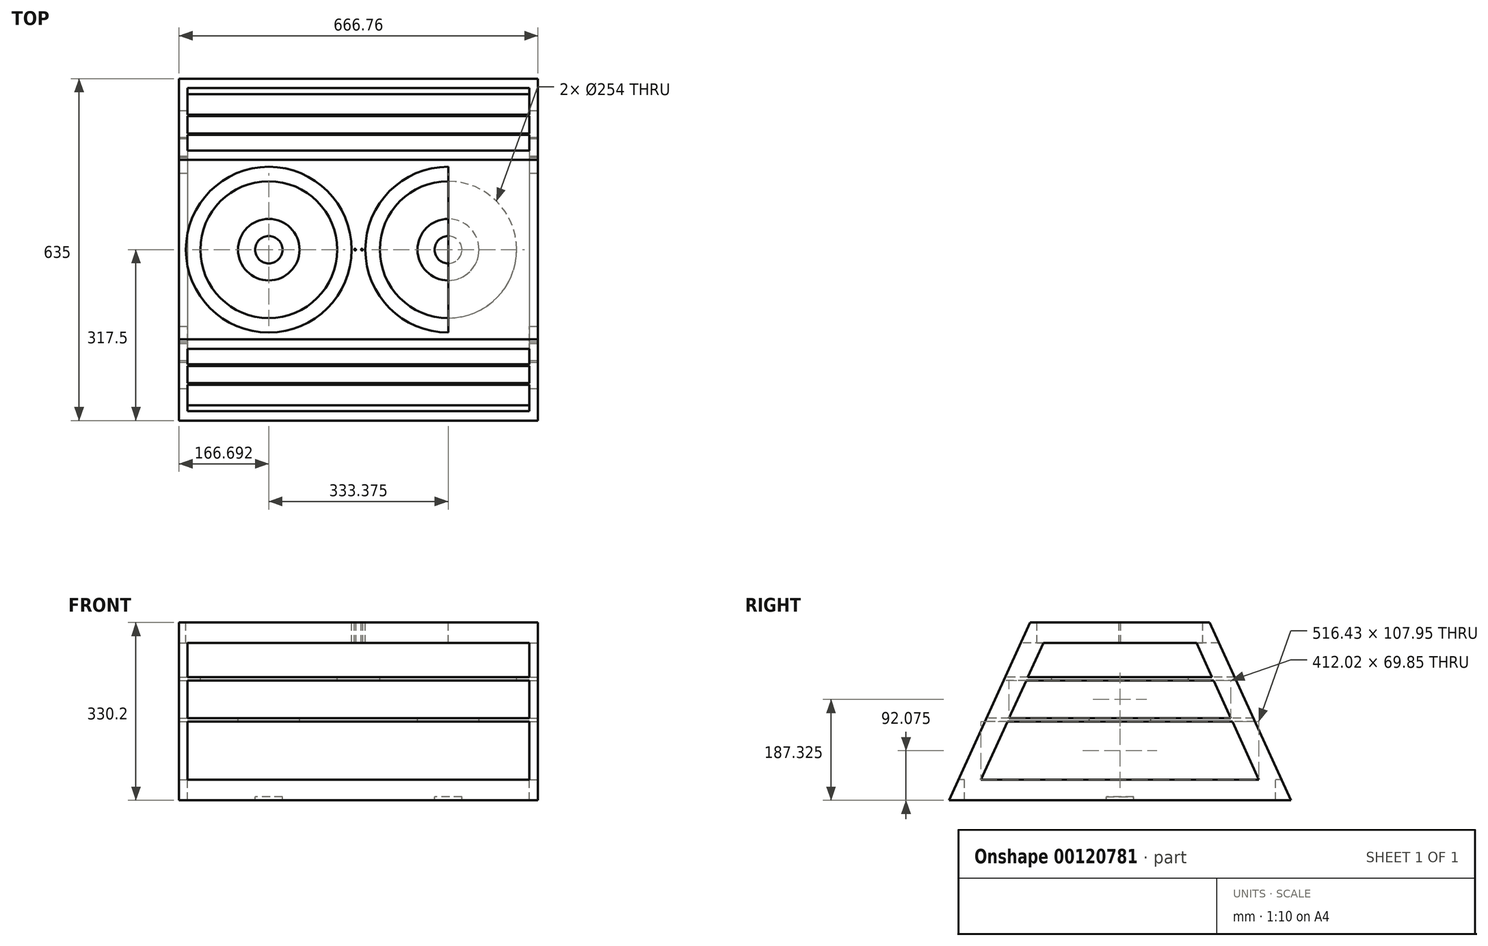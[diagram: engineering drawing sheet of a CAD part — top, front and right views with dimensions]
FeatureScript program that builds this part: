
annotation { "Feature Type Name" : "Feature", "Feature Type Description" : "" }
export const myFeature = defineFeature(function(context is Context, id is Id, definition is map)
    precondition{}
    {
        {
            var Q0;
            Q0=qCreatedBy(makeId("Top.planeOp"),FACE);
            var sketch = newSketch(context, id + "F0", { "sketchPlane" : qUnion([Q0])});
            skLineSegment(sketch, "E0.bottom", {"start": v(-333.38, 317.5) * mm, "end": v(333.38, 317.5) * mm});
            skLineSegment(sketch, "E0.top", {"start": v(-333.38, -317.5) * mm, "end": v(333.38, -317.5) * mm});
            skLineSegment(sketch, "E0.left", {"start": v(-333.38, 317.5) * mm, "end": v(-333.38, -317.5) * mm});
            skLineSegment(sketch, "E0.right", {"start": v(333.38, 317.5) * mm, "end": v(333.38, -317.5) * mm});
            skPoint(sketch, "E0.middle", {"position": v(0, 0) * mm});
            skSolve(sketch);
        }
        {
            var Q0;
            Q0 = qSketchRegion(id + "F0", true);
            extrude(context, id + "F1", {"entities" : qUnion([Q0]), "endBound" : BoundingType.SYMMETRIC, "depth" : 330.2 * mm});
        }
        {
            var Q0;
            Q0=makeQuery(id+"F1.opExtrude","CAP_FACE",FACE,{"disambiguationData":[OSD([sQuery(id+"F0.wireOp",EDGE,"E0.bottom"),sQuery(id+"F0.wireOp",EDGE,"E0.top"),sQuery(id+"F0.wireOp",EDGE,"E0.left"),sQuery(id+"F0.wireOp",EDGE,"E0.right")])],"isStart":false});
            var sketch = newSketch(context, id + "F2", { "sketchPlane" : qUnion([Q0])});
            skSolve(sketch);
        }
        {
            var Q0;
            Q0=makeQuery(id+"F2.imprint","IMPRINT",FACE,{"disambiguationData":[TD([[makeQuery(id+"F2.imprint","IMPRINT",EDGE,{"derivedFrom":makeQuery(id+"F1.opExtrude","CAP_EDGE",EDGE,{"disambiguationData":[OSD([sQuery(id+"F0.wireOp",EDGE,"E0.bottom")])],"isStart":false})}),-1.0]])]});
            var sketch = newSketch(context, id + "F3", { "sketchPlane" : qUnion([Q0])});
            skLineSegment(sketch, "E1.bottom", {"start": v(333.38, -166.69) * mm, "end": v(-333.38, -166.69) * mm});
            skLineSegment(sketch, "E1.top", {"start": v(333.38, 166.69) * mm, "end": v(-333.38, 166.69) * mm});
            skLineSegment(sketch, "E1.left", {"start": v(333.38, -166.69) * mm, "end": v(333.38, 166.69) * mm});
            skLineSegment(sketch, "E1.right", {"start": v(-333.38, -166.69) * mm, "end": v(-333.38, 166.69) * mm});
            skPoint(sketch, "E1.middle", {"position": v(0, 0) * mm});
            skLineSegment(sketch, "E2.bottom", {"start": v(166.69, -166.69) * mm, "end": v(-166.69, -166.69) * mm});
            skLineSegment(sketch, "E2.top", {"start": v(166.69, 166.69) * mm, "end": v(-166.69, 166.69) * mm});
            skLineSegment(sketch, "E2.left", {"start": v(166.69, -166.69) * mm, "end": v(166.69, 166.69) * mm});
            skLineSegment(sketch, "E2.right", {"start": v(-166.69, -166.69) * mm, "end": v(-166.69, 166.69) * mm});
            skCircle(sketch, "E3", {"center": v(-166.69, 0) * mm, "radius": 153.99 * mm});
            skCircle(sketch, "E4", {"center": v(166.69, 0) * mm, "radius": 153.99 * mm});
            skSolve(sketch);
        }
        {
            var Q0;
            Q0=makeQuery(id+"F1.opExtrude","SWEPT_FACE",FACE,{"disambiguationData":[OSD([sQuery(id+"F0.wireOp",EDGE,"E0.right")])]});
            var sketch = newSketch(context, id + "F4", { "sketchPlane" : qUnion([Q0])});
            skLineSegment(sketch, "E5.bottom", {"start": v(-166.69, 165.1) * mm, "end": v(166.69, 165.1) * mm});
            skLineSegment(sketch, "E5.top", {"start": v(-166.69, -165.1) * mm, "end": v(166.69, -165.1) * mm});
            skLineSegment(sketch, "E5.left", {"start": v(-166.69, 165.1) * mm, "end": v(-166.69, -165.1) * mm});
            skLineSegment(sketch, "E5.right", {"start": v(166.69, 165.1) * mm, "end": v(166.69, -165.1) * mm});
            skPoint(sketch, "E5.middle", {"position": v(0, 0) * mm});
            skLineSegment(sketch, "E6", {"start": v(-166.69, 165.1) * mm, "end": v(-317.5, -165.1) * mm});
            skLineSegment(sketch, "E7", {"start": v(166.69, 165.1) * mm, "end": v(317.5, -165.1) * mm});
            skLineSegment(sketch, "E8", {"start": v(-275.61, -165.1) * mm, "end": v(-124.8, 165.1) * mm});
            skLineSegment(sketch, "E9", {"start": v(-258.21, -127) * mm, "end": v(0, -127) * mm});
            skLineSegment(sketch, "E10", {"start": v(-184.09, 127) * mm, "end": v(0, 127) * mm});
            skPoint(sketch, "E10.endSnap0", {"position": v(0, 165.1) * mm});
            skLineSegment(sketch, "E11.MirrorCS", {"start": v(275.61, -165.1) * mm, "end": v(124.8, 165.1) * mm});
            skLineSegment(sketch, "E12.MirrorCS", {"start": v(258.21, -127) * mm, "end": v(0, -127) * mm});
            skLineSegment(sketch, "E13.MirrorCS", {"start": v(184.09, 127) * mm, "end": v(0, 127) * mm});
            skLineSegment(sketch, "E14.bottom", {"start": v(-213.1, 63.5) * mm, "end": v(213.1, 63.5) * mm});
            skLineSegment(sketch, "E14.top", {"start": v(-213.1, 57.15) * mm, "end": v(213.1, 57.15) * mm});
            skLineSegment(sketch, "E14.left", {"start": v(-213.1, 63.5) * mm, "end": v(-213.1, 57.15) * mm});
            skLineSegment(sketch, "E14.right", {"start": v(213.1, 63.5) * mm, "end": v(213.1, 57.15) * mm});
            skPoint(sketch, "E14.middle", {"position": v(0, 60.33) * mm});
            skLineSegment(sketch, "E15", {"start": v(0, 0) * mm, "end": v(0, -10.6) * mm});
            skLineSegment(sketch, "E16.bottom", {"start": v(242.7, -19.05) * mm, "end": v(-242.7, -19.05) * mm});
            skLineSegment(sketch, "E16.top", {"start": v(242.7, -12.7) * mm, "end": v(-242.7, -12.7) * mm});
            skLineSegment(sketch, "E16.left", {"start": v(242.7, -19.05) * mm, "end": v(242.7, -12.7) * mm});
            skLineSegment(sketch, "E16.right", {"start": v(-242.7, -19.05) * mm, "end": v(-242.7, -12.7) * mm});
            skPoint(sketch, "E16.middle", {"position": v(0, -15.87) * mm});
            skSolve(sketch);
        }
        {
            var Q0;
            {var subQ7=sQuery(id+"F4.wireOp",EDGE,"E8");var subQ9=sQuery(id+"F4.wireOp",EDGE,"E5.left");var subQ10=makeQuery(id+"F4.imprint","INTERSECT",VERTEX,{"derivedFrom":[subQ9,subQ7]});Q0=makeQuery(id+"F4.imprint","IMPRINT",FACE,{"disambiguationData":[TD([[makeQuery(id+"F4.imprint","IMPRINT",EDGE,{"disambiguationData":[TD([[subQ10,-1.0]])],"derivedFrom":subQ9}),1.0]])]});}
            var Q1;
            {var subQ0=sQuery(id+"F4.wireOp",EDGE,"E8");var subQ1=sQuery(id+"F4.wireOp",EDGE,"E5.left");var subQ2=makeQuery(id+"F4.imprint","INTERSECT",VERTEX,{"derivedFrom":[subQ1,subQ0]});Q1=makeQuery(id+"F4.imprint","IMPRINT",FACE,{"disambiguationData":[TD([[makeQuery(id+"F4.imprint","IMPRINT",EDGE,{"disambiguationData":[TD([[subQ2,-1.0]])],"derivedFrom":subQ1}),-1.0]])]});}
            var Q2;
            {var subQ0=sQuery(id+"F4.wireOp",EDGE,"E14.bottom");var subQ1=sQuery(id+"F4.wireOp",EDGE,"E11.MirrorCS");var subQ2=makeQuery(id+"F4.imprint","INTERSECT",VERTEX,{"derivedFrom":[subQ1,subQ0]});Q2=makeQuery(id+"F4.imprint","IMPRINT",FACE,{"disambiguationData":[TD([[makeQuery(id+"F4.imprint","IMPRINT",EDGE,{"disambiguationData":[TD([[subQ2,-1.0]])],"derivedFrom":subQ1}),1.0]])]});}
            var Q3;
            {var subQ0=sQuery(id+"F4.wireOp",EDGE,"E16.top");var subQ1=sQuery(id+"F4.wireOp",EDGE,"E11.MirrorCS");var subQ2=makeQuery(id+"F4.imprint","INTERSECT",VERTEX,{"derivedFrom":[subQ1,subQ0]});Q3=makeQuery(id+"F4.imprint","IMPRINT",FACE,{"disambiguationData":[TD([[makeQuery(id+"F4.imprint","IMPRINT",EDGE,{"disambiguationData":[TD([[subQ2,-1.0]])],"derivedFrom":subQ1}),1.0]])]});}
            var Q4;
            {var subQ0=sQuery(id+"F4.wireOp",EDGE,"E14.top");var subQ1=sQuery(id+"F4.wireOp",EDGE,"E5.left");var subQ2=makeQuery(id+"F4.imprint","INTERSECT",VERTEX,{"derivedFrom":[subQ1,subQ0]});Q4=makeQuery(id+"F4.imprint","IMPRINT",FACE,{"disambiguationData":[TD([[makeQuery(id+"F4.imprint","IMPRINT",EDGE,{"disambiguationData":[TD([[subQ2,-1.0]])],"derivedFrom":subQ1}),1.0]])]});}
            var Q5;
            {var subQ0=sQuery(id+"F4.wireOp",EDGE,"E14.top");var subQ1=sQuery(id+"F4.wireOp",EDGE,"E5.left");var subQ2=makeQuery(id+"F4.imprint","INTERSECT",VERTEX,{"derivedFrom":[subQ1,subQ0]});Q5=makeQuery(id+"F4.imprint","IMPRINT",FACE,{"disambiguationData":[TD([[makeQuery(id+"F4.imprint","IMPRINT",EDGE,{"disambiguationData":[TD([[subQ2,-1.0]])],"derivedFrom":subQ1}),-1.0]])]});}
            var Q6;
            {var subQ0=sQuery(id+"F4.wireOp",EDGE,"E16.bottom");var subQ1=sQuery(id+"F4.wireOp",EDGE,"E5.left");var subQ2=makeQuery(id+"F4.imprint","INTERSECT",VERTEX,{"derivedFrom":[subQ1,subQ0]});Q6=makeQuery(id+"F4.imprint","IMPRINT",FACE,{"disambiguationData":[TD([[makeQuery(id+"F4.imprint","IMPRINT",EDGE,{"disambiguationData":[TD([[subQ2,-1.0]])],"derivedFrom":subQ1}),-1.0]])]});}
            var Q7;
            {var subQ5=sQuery(id+"F4.wireOp",EDGE,"E5.left");var subQ7=sQuery(id+"F4.wireOp",EDGE,"E16.bottom");var subQ8=makeQuery(id+"F4.imprint","INTERSECT",VERTEX,{"derivedFrom":[subQ5,subQ7]});Q7=makeQuery(id+"F4.imprint","IMPRINT",FACE,{"disambiguationData":[TD([[makeQuery(id+"F4.imprint","IMPRINT",EDGE,{"disambiguationData":[TD([[subQ8,-1.0]])],"derivedFrom":subQ5}),1.0]])]});}
            var Q8;
            {var subQ0=sQuery(id+"F4.wireOp",EDGE,"E12.MirrorCS");var subQ1=sQuery(id+"F4.wireOp",EDGE,"E11.MirrorCS");var subQ2=makeQuery(id+"F4.imprint","INTERSECT",VERTEX,{"derivedFrom":[subQ1,subQ0]});Q8=makeQuery(id+"F4.imprint","IMPRINT",FACE,{"disambiguationData":[TD([[makeQuery(id+"F4.imprint","IMPRINT",EDGE,{"disambiguationData":[TD([[subQ2,-1.0]])],"derivedFrom":subQ1}),1.0]])]});}
            var Q9;
            {var subQ0=sQuery(id+"F0.wireOp",EDGE,"E0.right");var subQ1=makeQuery(id+"F1.opExtrude","SWEPT_EDGE",EDGE,{"disambiguationData":[OSD([sQuery(id+"F0.wireOp",EDGE,"E0.bottom"),subQ0])]});Q9=makeQuery(id+"F4.imprint","IMPRINT",FACE,{"disambiguationData":[TD([[makeQuery(id+"F4.imprint","IMPRINT",EDGE,{"derivedFrom":subQ1}),-1.0]])]});}
            var Q10;
            {var subQ3=sQuery(id+"F0.wireOp",EDGE,"E0.right");var subQ4=makeQuery(id+"F1.opExtrude","SWEPT_EDGE",EDGE,{"disambiguationData":[OSD([sQuery(id+"F0.wireOp",EDGE,"E0.top"),subQ3])]});Q10=makeQuery(id+"F4.imprint","IMPRINT",FACE,{"disambiguationData":[TD([[makeQuery(id+"F4.imprint","IMPRINT",EDGE,{"derivedFrom":subQ4}),1.0]])]});}
            extrude(context, id + "F5", {"entities" : qUnion([Q0, Q1, Q2, Q3, Q4, Q5, Q6, Q7, Q8, Q9, Q10]), "operationType" : NewBodyOperationType.REMOVE, "endBound" : BoundingType.THROUGH_ALL, "oppositeDirection" : true, "depth" : 25.4 * mm});
        }
        {
            var Q0;
            Q0=qCreatedBy(makeId("Front.planeOp"),FACE);
            var sketch = newSketch(context, id + "F6", { "sketchPlane" : qUnion([Q0])});
            skLineSegment(sketch, "E17.bottom", {"start": v(-317.5, 127) * mm, "end": v(317.5, 127) * mm});
            skLineSegment(sketch, "E17.top", {"start": v(-317.5, -127) * mm, "end": v(317.5, -127) * mm});
            skLineSegment(sketch, "E17.left", {"start": v(-317.5, 127) * mm, "end": v(-317.5, -127) * mm});
            skLineSegment(sketch, "E17.right", {"start": v(317.5, 127) * mm, "end": v(317.5, -127) * mm});
            skPoint(sketch, "E17.middle", {"position": v(0, 0) * mm});
            skLineSegment(sketch, "E18.bottom", {"start": v(-317.5, 63.5) * mm, "end": v(317.5, 63.5) * mm});
            skLineSegment(sketch, "E18.top", {"start": v(-317.5, 57.15) * mm, "end": v(317.5, 57.15) * mm});
            skLineSegment(sketch, "E18.left", {"start": v(-317.5, 63.5) * mm, "end": v(-317.5, 57.15) * mm});
            skLineSegment(sketch, "E18.right", {"start": v(317.5, 63.5) * mm, "end": v(317.5, 57.15) * mm});
            skPoint(sketch, "E18.middle", {"position": v(0, 60.32) * mm});
            skLineSegment(sketch, "E19.bottom", {"start": v(-317.5, -12.7) * mm, "end": v(317.5, -12.7) * mm});
            skLineSegment(sketch, "E19.top", {"start": v(-317.5, -19.05) * mm, "end": v(317.5, -19.05) * mm});
            skLineSegment(sketch, "E19.left", {"start": v(-317.5, -12.7) * mm, "end": v(-317.5, -19.05) * mm});
            skLineSegment(sketch, "E19.right", {"start": v(317.5, -12.7) * mm, "end": v(317.5, -19.05) * mm});
            skPoint(sketch, "E19.middle", {"position": v(0, -15.87) * mm});
            skSolve(sketch);
        }
        {
            var Q0;
            {var subQ0=sQuery(id+"F6.wireOp",EDGE,"E17.bottom");Q0=makeQuery(id+"F6.imprint","IMPRINT",FACE,{"disambiguationData":[TD([[makeQuery(id+"F6.imprint","IMPRINT",EDGE,{"derivedFrom":subQ0}),-1.0]])]});}
            var Q1;
            {var subQ0=sQuery(id+"F6.wireOp",EDGE,"E17.top");Q1=makeQuery(id+"F6.imprint","IMPRINT",FACE,{"disambiguationData":[TD([[makeQuery(id+"F6.imprint","IMPRINT",EDGE,{"derivedFrom":subQ0}),1.0]])]});}
            var Q2;
            {var subQ0=sQuery(id+"F6.wireOp",EDGE,"E18.top");Q2=makeQuery(id+"F6.imprint","IMPRINT",FACE,{"disambiguationData":[TD([[makeQuery(id+"F6.imprint","IMPRINT",EDGE,{"derivedFrom":subQ0}),-1.0]])]});}
            extrude(context, id + "F7", {"entities" : qUnion([Q0, Q1, Q2]), "operationType" : NewBodyOperationType.REMOVE, "endBound" : BoundingType.SYMMETRIC, "oppositeDirection" : true, "depth" : 660.4 * mm});
        }
        {
            var Q0;
            {var subQ10=sQuery(id+"F3.wireOp",EDGE,"E2.bottom");Q0=makeQuery(id+"F3.imprint","IMPRINT",FACE,{"disambiguationData":[TD([[makeQuery(id+"F3.imprint","IMPRINT",EDGE,{"derivedFrom":subQ10}),-1.0]])]});}
            var sketch = newSketch(context, id + "F8", { "sketchPlane" : qUnion([Q0])});
            skLineSegment(sketch, "E20.bottom", {"start": v(166.69, -166.69) * mm, "end": v(-166.69, -166.69) * mm});
            skLineSegment(sketch, "E20.top", {"start": v(166.69, 166.69) * mm, "end": v(-166.69, 166.69) * mm});
            skLineSegment(sketch, "E20.left", {"start": v(166.69, -166.69) * mm, "end": v(166.69, 166.69) * mm});
            skLineSegment(sketch, "E20.right", {"start": v(-166.69, -166.69) * mm, "end": v(-166.69, 166.69) * mm});
            skPoint(sketch, "E20.middle", {"position": v(0, 0) * mm});
            skCircle(sketch, "E21", {"center": v(-166.69, 0) * mm, "radius": 153.99 * mm});
            skCircle(sketch, "E22", {"center": v(166.69, 0) * mm, "radius": 153.99 * mm});
            skSolve(sketch);
        }
        {
            var Q0;
            {var subQ0=sQuery(id+"F3.wireOp",EDGE,"E3");var subQ1=sQuery(id+"F3.wireOp",EDGE,"E2.right");var subQ2=makeQuery(id+"F3.imprint","INTERSECT",VERTEX,{"disambiguationData":[OD(0.0)],"derivedFrom":[subQ1,subQ0]});Q0=makeQuery(id+"F3.imprint","IMPRINT",FACE,{"disambiguationData":[TD([[makeQuery(id+"F3.imprint","IMPRINT",EDGE,{"disambiguationData":[TD([[subQ2,-1.0]])],"derivedFrom":subQ1}),1.0]])]});}
            var Q1;
            {var subQ0=sQuery(id+"F3.wireOp",EDGE,"E3");var subQ1=sQuery(id+"F3.wireOp",EDGE,"E2.right");var subQ2=makeQuery(id+"F3.imprint","INTERSECT",VERTEX,{"disambiguationData":[OD(0.0)],"derivedFrom":[subQ1,subQ0]});Q1=makeQuery(id+"F3.imprint","IMPRINT",FACE,{"disambiguationData":[TD([[makeQuery(id+"F3.imprint","IMPRINT",EDGE,{"disambiguationData":[TD([[subQ2,-1.0]])],"derivedFrom":subQ1}),-1.0]])]});}
            var Q2;
            {var subQ0=sQuery(id+"F3.wireOp",EDGE,"E4");var subQ1=sQuery(id+"F3.wireOp",EDGE,"E2.left");var subQ2=makeQuery(id+"F3.imprint","INTERSECT",VERTEX,{"disambiguationData":[OD(0.0)],"derivedFrom":[subQ1,subQ0]});Q2=makeQuery(id+"F3.imprint","IMPRINT",FACE,{"disambiguationData":[TD([[makeQuery(id+"F3.imprint","IMPRINT",EDGE,{"disambiguationData":[TD([[subQ2,-1.0]])],"derivedFrom":subQ1}),1.0]])]});}
            var Q3;
            {var subQ0=sQuery(id+"F8.wireOp",EDGE,"E22");var subQ1=sQuery(id+"F8.wireOp",EDGE,"E20.left");var subQ2=makeQuery(id+"F8.imprint","INTERSECT",VERTEX,{"disambiguationData":[OD(0.0)],"derivedFrom":[subQ1,subQ0]});Q3=makeQuery(id+"F8.imprint","IMPRINT",FACE,{"disambiguationData":[TD([[makeQuery(id+"F8.imprint","IMPRINT",EDGE,{"disambiguationData":[TD([[subQ2,-1.0]])],"derivedFrom":subQ1}),-1.0]])]});}
            extrude(context, id + "F9", {"entities" : qUnion([Q0, Q1, Q2, Q3]), "operationType" : NewBodyOperationType.REMOVE, "oppositeDirection" : true, "depth" : 38.1 * mm});
        }
        {
            var Q0;
            Q0=makeQuery(id+"F7.boolean.opBoolean","MERGE",FACE,{"derivedFrom":[makeQuery(id+"F5.boolean.opBoolean","COPY",FACE,{"derivedFrom":makeQuery(id+"F5.opExtrude","SWEPT_FACE",FACE,{"disambiguationData":[OSD([sQuery(id+"F4.wireOp",EDGE,"E14.bottom")])]})}),makeQuery(id+"F7.opExtrude","SWEPT_FACE",FACE,{"disambiguationData":[OSD([sQuery(id+"F6.wireOp",EDGE,"E18.bottom")])]})]});
            var sketch = newSketch(context, id + "F10", { "sketchPlane" : qUnion([Q0])});
            skLineSegment(sketch, "E23.bottom", {"start": v(166.69, -166.69) * mm, "end": v(-166.69, -166.69) * mm});
            skLineSegment(sketch, "E23.top", {"start": v(166.69, 166.69) * mm, "end": v(-166.69, 166.69) * mm});
            skLineSegment(sketch, "E23.left", {"start": v(166.69, -166.69) * mm, "end": v(166.69, 166.69) * mm});
            skLineSegment(sketch, "E23.right", {"start": v(-166.69, -166.69) * mm, "end": v(-166.69, 166.69) * mm});
            skPoint(sketch, "E23.middle", {"position": v(0, 0) * mm});
            skCircle(sketch, "E24", {"center": v(-166.69, 0) * mm, "radius": 127 * mm});
            skCircle(sketch, "E25", {"center": v(166.69, 0) * mm, "radius": 127 * mm});
            skSolve(sketch);
        }
        {
            var Q0;
            {var subQ0=sQuery(id+"F10.wireOp",EDGE,"E24");var subQ1=sQuery(id+"F10.wireOp",EDGE,"E23.right");var subQ2=makeQuery(id+"F10.imprint","INTERSECT",VERTEX,{"disambiguationData":[OD(0.0)],"derivedFrom":[subQ1,subQ0]});Q0=makeQuery(id+"F10.imprint","IMPRINT",FACE,{"disambiguationData":[TD([[makeQuery(id+"F10.imprint","IMPRINT",EDGE,{"disambiguationData":[TD([[subQ2,-1.0]])],"derivedFrom":subQ1}),1.0]])]});}
            var Q1;
            {var subQ0=sQuery(id+"F10.wireOp",EDGE,"E24");var subQ1=sQuery(id+"F10.wireOp",EDGE,"E23.right");var subQ2=makeQuery(id+"F10.imprint","INTERSECT",VERTEX,{"disambiguationData":[OD(0.0)],"derivedFrom":[subQ1,subQ0]});Q1=makeQuery(id+"F10.imprint","IMPRINT",FACE,{"disambiguationData":[TD([[makeQuery(id+"F10.imprint","IMPRINT",EDGE,{"disambiguationData":[TD([[subQ2,-1.0]])],"derivedFrom":subQ1}),-1.0]])]});}
            var Q2;
            {var subQ0=sQuery(id+"F10.wireOp",EDGE,"E25");var subQ1=sQuery(id+"F10.wireOp",EDGE,"E23.left");var subQ2=makeQuery(id+"F10.imprint","INTERSECT",VERTEX,{"disambiguationData":[OD(0.0)],"derivedFrom":[subQ1,subQ0]});Q2=makeQuery(id+"F10.imprint","IMPRINT",FACE,{"disambiguationData":[TD([[makeQuery(id+"F10.imprint","IMPRINT",EDGE,{"disambiguationData":[TD([[subQ2,-1.0]])],"derivedFrom":subQ1}),1.0]])]});}
            var Q3;
            {var subQ0=sQuery(id+"F10.wireOp",EDGE,"E25");var subQ1=sQuery(id+"F10.wireOp",EDGE,"E23.left");var subQ2=makeQuery(id+"F10.imprint","INTERSECT",VERTEX,{"disambiguationData":[OD(0.0)],"derivedFrom":[subQ1,subQ0]});Q3=makeQuery(id+"F10.imprint","IMPRINT",FACE,{"disambiguationData":[TD([[makeQuery(id+"F10.imprint","IMPRINT",EDGE,{"disambiguationData":[TD([[subQ2,-1.0]])],"derivedFrom":subQ1}),-1.0]])]});}
            extrude(context, id + "F11", {"entities" : qUnion([Q0, Q1, Q2, Q3]), "operationType" : NewBodyOperationType.REMOVE, "oppositeDirection" : true, "depth" : 25.4 * mm});
        }
        {
            var Q0;
            Q0=makeQuery(id+"F7.boolean.opBoolean","MERGE",FACE,{"derivedFrom":[makeQuery(id+"F5.boolean.opBoolean","COPY",FACE,{"derivedFrom":makeQuery(id+"F5.opExtrude","SWEPT_FACE",FACE,{"disambiguationData":[OSD([sQuery(id+"F4.wireOp",EDGE,"E16.top")])]})}),makeQuery(id+"F7.opExtrude","SWEPT_FACE",FACE,{"disambiguationData":[OSD([sQuery(id+"F6.wireOp",EDGE,"E19.bottom")])]})]});
            var sketch = newSketch(context, id + "F12", { "sketchPlane" : qUnion([Q0])});
            skLineSegment(sketch, "E26.bottom", {"start": v(166.69, -166.69) * mm, "end": v(-166.69, -166.69) * mm});
            skLineSegment(sketch, "E26.top", {"start": v(166.69, 166.69) * mm, "end": v(-166.69, 166.69) * mm});
            skLineSegment(sketch, "E26.left", {"start": v(166.69, -166.69) * mm, "end": v(166.69, 166.69) * mm});
            skLineSegment(sketch, "E26.right", {"start": v(-166.69, -166.69) * mm, "end": v(-166.69, 166.69) * mm});
            skPoint(sketch, "E26.middle", {"position": v(0, 0) * mm});
            skCircle(sketch, "E27", {"center": v(-166.69, 0) * mm, "radius": 57.15 * mm});
            skCircle(sketch, "E28", {"center": v(166.69, 0) * mm, "radius": 57.15 * mm});
            skSolve(sketch);
        }
        {
            var Q0;
            {var subQ0=sQuery(id+"F12.wireOp",EDGE,"E27");var subQ1=sQuery(id+"F12.wireOp",EDGE,"E26.right");var subQ2=makeQuery(id+"F12.imprint","INTERSECT",VERTEX,{"disambiguationData":[OD(0.0)],"derivedFrom":[subQ1,subQ0]});Q0=makeQuery(id+"F12.imprint","IMPRINT",FACE,{"disambiguationData":[TD([[makeQuery(id+"F12.imprint","IMPRINT",EDGE,{"disambiguationData":[TD([[subQ2,-1.0]])],"derivedFrom":subQ1}),1.0]])]});}
            var Q1;
            {var subQ0=sQuery(id+"F12.wireOp",EDGE,"E27");var subQ1=sQuery(id+"F12.wireOp",EDGE,"E26.right");var subQ2=makeQuery(id+"F12.imprint","INTERSECT",VERTEX,{"disambiguationData":[OD(0.0)],"derivedFrom":[subQ1,subQ0]});Q1=makeQuery(id+"F12.imprint","IMPRINT",FACE,{"disambiguationData":[TD([[makeQuery(id+"F12.imprint","IMPRINT",EDGE,{"disambiguationData":[TD([[subQ2,-1.0]])],"derivedFrom":subQ1}),-1.0]])]});}
            var Q2;
            {var subQ0=sQuery(id+"F12.wireOp",EDGE,"E28");var subQ1=sQuery(id+"F12.wireOp",EDGE,"E26.left");var subQ2=makeQuery(id+"F12.imprint","INTERSECT",VERTEX,{"disambiguationData":[OD(0.0)],"derivedFrom":[subQ1,subQ0]});Q2=makeQuery(id+"F12.imprint","IMPRINT",FACE,{"disambiguationData":[TD([[makeQuery(id+"F12.imprint","IMPRINT",EDGE,{"disambiguationData":[TD([[subQ2,-1.0]])],"derivedFrom":subQ1}),1.0]])]});}
            var Q3;
            {var subQ0=sQuery(id+"F12.wireOp",EDGE,"E28");var subQ1=sQuery(id+"F12.wireOp",EDGE,"E26.left");var subQ2=makeQuery(id+"F12.imprint","INTERSECT",VERTEX,{"disambiguationData":[OD(0.0)],"derivedFrom":[subQ1,subQ0]});Q3=makeQuery(id+"F12.imprint","IMPRINT",FACE,{"disambiguationData":[TD([[makeQuery(id+"F12.imprint","IMPRINT",EDGE,{"disambiguationData":[TD([[subQ2,-1.0]])],"derivedFrom":subQ1}),-1.0]])]});}
            extrude(context, id + "F13", {"entities" : qUnion([Q0, Q1, Q2, Q3]), "operationType" : NewBodyOperationType.REMOVE, "oppositeDirection" : true, "depth" : 25.4 * mm});
        }
        {
            var Q0;
            Q0=makeQuery(id+"F7.boolean.opBoolean","MERGE",FACE,{"derivedFrom":[makeQuery(id+"F5.boolean.opBoolean","COPY",FACE,{"derivedFrom":makeQuery(id+"F5.opExtrude","SWEPT_FACE",FACE,{"disambiguationData":[OSD([sQuery(id+"F4.wireOp",EDGE,"E9"),sQuery(id+"F4.wireOp",EDGE,"E12.MirrorCS")])]})}),makeQuery(id+"F7.opExtrude","SWEPT_FACE",FACE,{"disambiguationData":[OSD([sQuery(id+"F6.wireOp",EDGE,"E17.top")])]})]});
            var sketch = newSketch(context, id + "F14", { "sketchPlane" : qUnion([Q0])});
            skLineSegment(sketch, "E29.bottom", {"start": v(317.5, -288.92) * mm, "end": v(-317.5, -288.92) * mm});
            skLineSegment(sketch, "E29.top", {"start": v(317.5, 288.92) * mm, "end": v(-317.5, 288.92) * mm});
            skLineSegment(sketch, "E29.left", {"start": v(317.5, -288.92) * mm, "end": v(317.5, 288.92) * mm});
            skLineSegment(sketch, "E29.right", {"start": v(-317.5, -288.92) * mm, "end": v(-317.5, 288.92) * mm});
            skPoint(sketch, "E29.middle", {"position": v(0, 0) * mm});
            skSolve(sketch);
        }
        {
            var Q0;
            Q0 = qSketchRegion(id + "F14", true);
            extrude(context, id + "F15", {"entities" : qUnion([Q0]), "operationType" : NewBodyOperationType.REMOVE, "oppositeDirection" : true, "depth" : 31.75 * mm});
        }
        {
            var Q0;
            Q0=makeQuery(id+"F15.boolean.opBoolean","COPY",FACE,{"derivedFrom":makeQuery(id+"F15.opExtrude","CAP_FACE",FACE,{"disambiguationData":[OSD([sQuery(id+"F14.wireOp",EDGE,"E29.bottom"),sQuery(id+"F14.wireOp",EDGE,"E29.top"),sQuery(id+"F14.wireOp",EDGE,"E29.left"),sQuery(id+"F14.wireOp",EDGE,"E29.right")])],"isStart":false})});
            var sketch = newSketch(context, id + "F16", { "sketchPlane" : qUnion([Q0])});
            skLineSegment(sketch, "E30.bottom", {"start": v(166.69, -166.69) * mm, "end": v(-166.69, -166.69) * mm});
            skLineSegment(sketch, "E30.top", {"start": v(166.69, 166.69) * mm, "end": v(-166.69, 166.69) * mm});
            skLineSegment(sketch, "E30.left", {"start": v(166.69, -166.69) * mm, "end": v(166.69, 166.69) * mm});
            skLineSegment(sketch, "E30.right", {"start": v(-166.69, -166.69) * mm, "end": v(-166.69, 166.69) * mm});
            skPoint(sketch, "E30.middle", {"position": v(0, 0) * mm});
            skCircle(sketch, "E31", {"center": v(-166.69, 0) * mm, "radius": 25.4 * mm});
            skCircle(sketch, "E32", {"center": v(166.69, 0) * mm, "radius": 25.4 * mm});
            skSolve(sketch);
        }
        {
            var Q0;
            {var subQ0=sQuery(id+"F16.wireOp",EDGE,"E31");var subQ1=sQuery(id+"F16.wireOp",EDGE,"E30.right");var subQ2=makeQuery(id+"F16.imprint","INTERSECT",VERTEX,{"disambiguationData":[OD(0.0)],"derivedFrom":[subQ1,subQ0]});Q0=makeQuery(id+"F16.imprint","IMPRINT",FACE,{"disambiguationData":[TD([[makeQuery(id+"F16.imprint","IMPRINT",EDGE,{"disambiguationData":[TD([[subQ2,-1.0]])],"derivedFrom":subQ1}),1.0]])]});}
            var Q1;
            {var subQ0=sQuery(id+"F16.wireOp",EDGE,"E31");var subQ1=sQuery(id+"F16.wireOp",EDGE,"E30.right");var subQ2=makeQuery(id+"F16.imprint","INTERSECT",VERTEX,{"disambiguationData":[OD(0.0)],"derivedFrom":[subQ1,subQ0]});Q1=makeQuery(id+"F16.imprint","IMPRINT",FACE,{"disambiguationData":[TD([[makeQuery(id+"F16.imprint","IMPRINT",EDGE,{"disambiguationData":[TD([[subQ2,-1.0]])],"derivedFrom":subQ1}),-1.0]])]});}
            var Q2;
            {var subQ0=sQuery(id+"F16.wireOp",EDGE,"E32");var subQ1=sQuery(id+"F16.wireOp",EDGE,"E30.left");var subQ2=makeQuery(id+"F16.imprint","INTERSECT",VERTEX,{"disambiguationData":[OD(0.0)],"derivedFrom":[subQ1,subQ0]});Q2=makeQuery(id+"F16.imprint","IMPRINT",FACE,{"disambiguationData":[TD([[makeQuery(id+"F16.imprint","IMPRINT",EDGE,{"disambiguationData":[TD([[subQ2,-1.0]])],"derivedFrom":subQ1}),-1.0]])]});}
            var Q3;
            {var subQ0=sQuery(id+"F16.wireOp",EDGE,"E32");var subQ1=sQuery(id+"F16.wireOp",EDGE,"E30.left");var subQ2=makeQuery(id+"F16.imprint","INTERSECT",VERTEX,{"disambiguationData":[OD(0.0)],"derivedFrom":[subQ1,subQ0]});Q3=makeQuery(id+"F16.imprint","IMPRINT",FACE,{"disambiguationData":[TD([[makeQuery(id+"F16.imprint","IMPRINT",EDGE,{"disambiguationData":[TD([[subQ2,-1.0]])],"derivedFrom":subQ1}),1.0]])]});}
            extrude(context, id + "F17", {"entities" : qUnion([Q0, Q1, Q2, Q3]), "operationType" : NewBodyOperationType.REMOVE, "oppositeDirection" : true, "depth" : 25.4 * mm});
        }
        {
            var Q0;
            Q0=makeQuery(id+"F2.imprint","IMPRINT",FACE,{"disambiguationData":[TD([[makeQuery(id+"F2.imprint","IMPRINT",EDGE,{"derivedFrom":makeQuery(id+"F1.opExtrude","CAP_EDGE",EDGE,{"disambiguationData":[OSD([sQuery(id+"F0.wireOp",EDGE,"E0.bottom")])],"isStart":false})}),-1.0]])]});
            var sketch = newSketch(context, id + "F18", { "sketchPlane" : qUnion([Q0])});
            skLineSegment(sketch, "E33", {"start": v(0, 7.37) * mm, "end": v(0, 0) * mm});
            skCircle(sketch, "E34", {"center": v(6.35, 0) * mm, "radius": 1.59 * mm});
            skCircle(sketch, "E35.MirrorC", {"center": v(-6.35, 0) * mm, "radius": 1.59 * mm});
            skSolve(sketch);
        }
        {
            var Q0;
            Q0=sQuery(id+"F18.wireOp",VERTEX,"E35.MirrorC.center");
            var Q1;
            Q1=sQuery(id+"F18.wireOp",VERTEX,"E34.center");
            var Q2;
            Q2=makeQuery(id+"F1.opExtrude","SWEPT_BODY",BODY,{"disambiguationData":[OSD([sQuery(id+"F0.wireOp",EDGE,"E0.bottom"),sQuery(id+"F0.wireOp",EDGE,"E0.top"),sQuery(id+"F0.wireOp",EDGE,"E0.left"),sQuery(id+"F0.wireOp",EDGE,"E0.right")])]});
            hole(context, id + "F19", {"style" : HoleStyle.SIMPLE, "endStyle" : HoleEndStyle.BLIND, "holeDiameter" : 3.17 * mm, "holeDepth" : 38.1 * mm, "locations" : qUnion([Q0, Q1]), "scope" : qUnion([Q2])});
        }
    });
